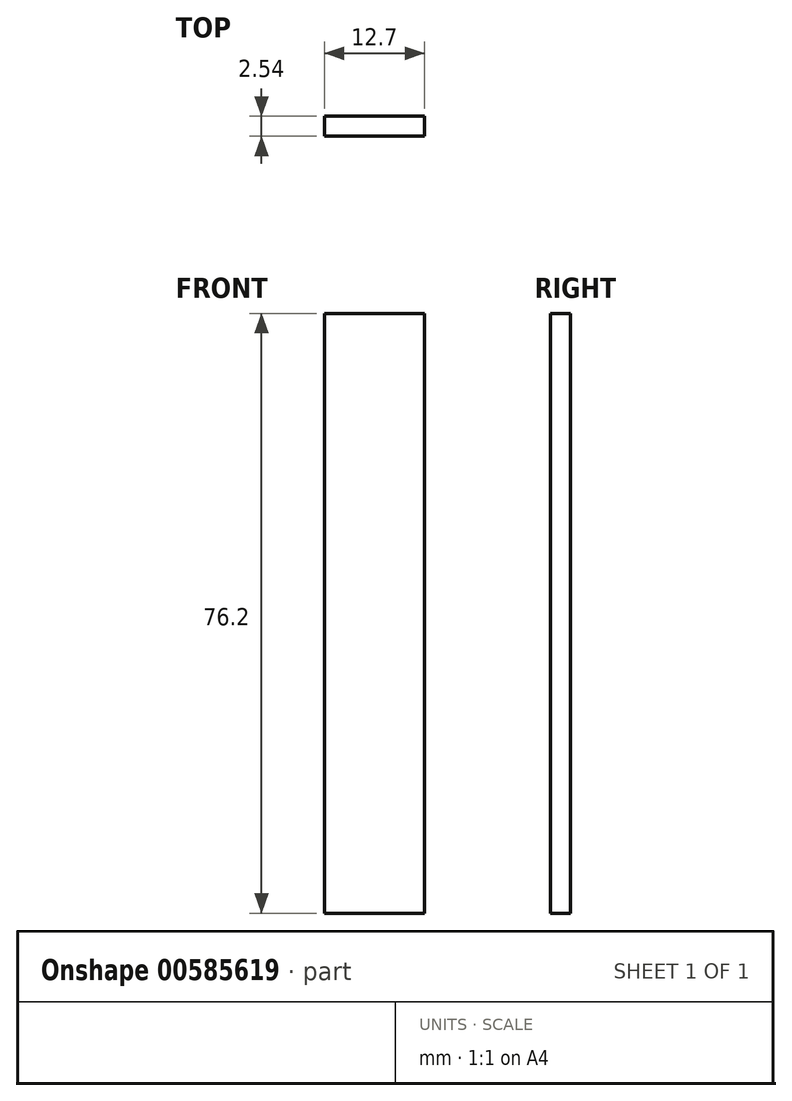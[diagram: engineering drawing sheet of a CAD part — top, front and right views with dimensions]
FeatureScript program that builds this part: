
annotation { "Feature Type Name" : "Feature", "Feature Type Description" : "" }
export const myFeature = defineFeature(function(context is Context, id is Id, definition is map)
    precondition{}
    {
        {
            var Q0;
            Q0=qCreatedBy(makeId("Top.planeOp"),FACE);
            var sketch = newSketch(context, id + "F0", { "sketchPlane" : qUnion([Q0])});
            skLineSegment(sketch, "E0.bottom", {"start": v(-6.35, 1.27) * mm, "end": v(6.35, 1.27) * mm});
            skLineSegment(sketch, "E0.top", {"start": v(-6.35, -1.27) * mm, "end": v(6.35, -1.27) * mm});
            skLineSegment(sketch, "E0.left", {"start": v(-6.35, 1.27) * mm, "end": v(-6.35, -1.27) * mm});
            skLineSegment(sketch, "E0.right", {"start": v(6.35, 1.27) * mm, "end": v(6.35, -1.27) * mm});
            skPoint(sketch, "E0.middle", {"position": v(0, 0) * mm});
            skSolve(sketch);
        }
        {
            var Q0;
            Q0=makeQuery(id+"F0.imprint","IMPRINT",FACE,{"disambiguationData":[TD([[makeQuery(id+"F0.imprint","IMPRINT",EDGE,{"derivedFrom":sQuery(id+"F0.wireOp",EDGE,"E0.bottom")}),-1.0]])]});
            extrude(context, id + "F1", {"entities" : qUnion([Q0]), "depth" : 76.2 * mm, "offsetDistance" : 25.4 * mm});
        }
    });
